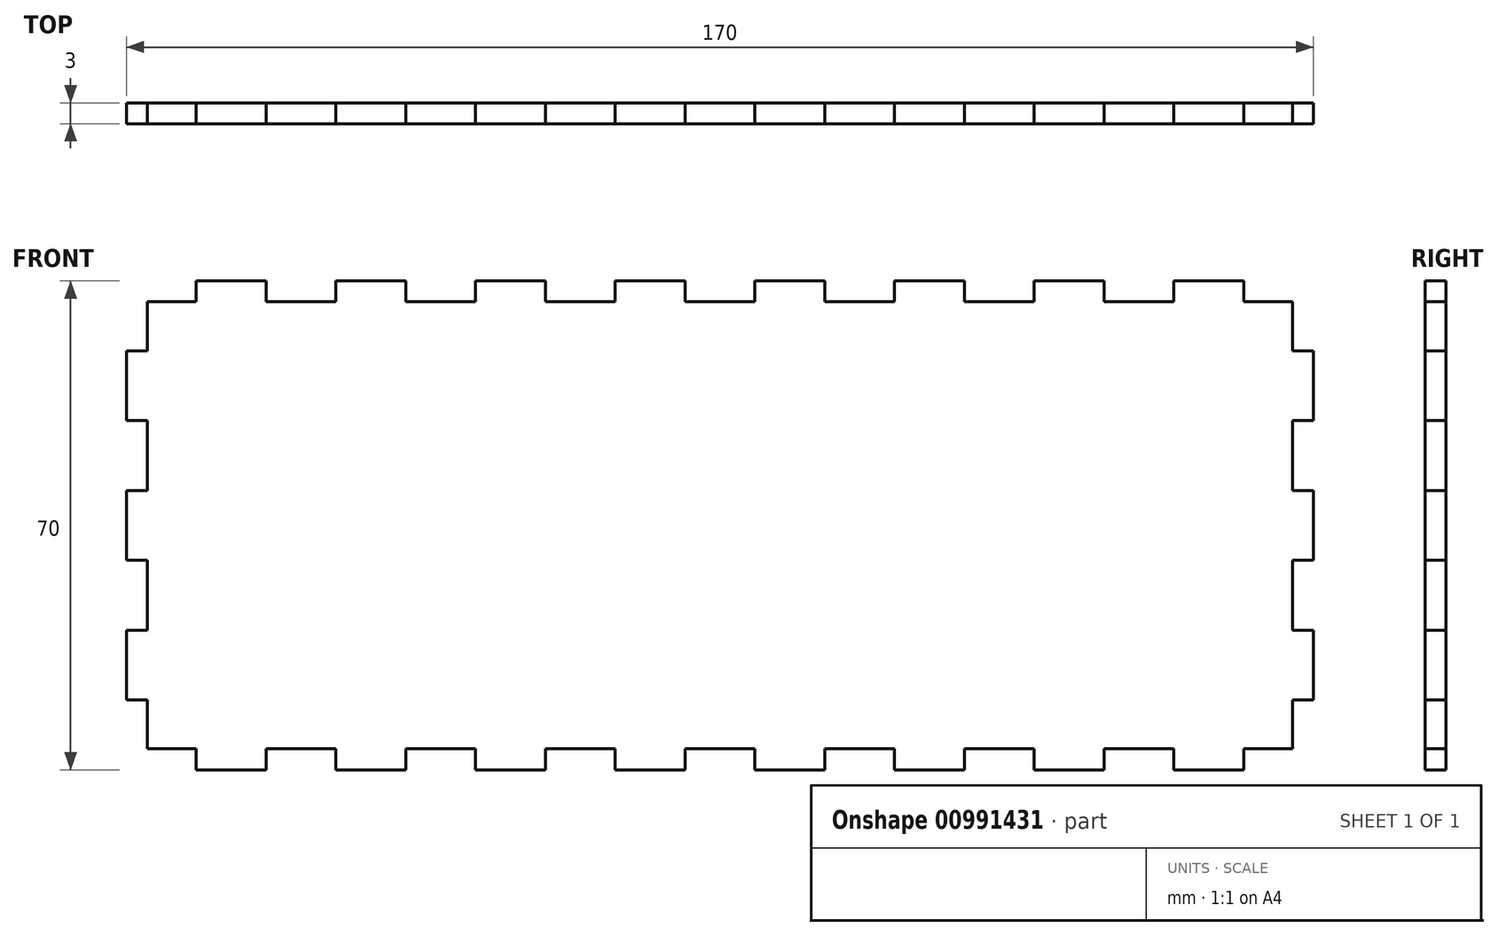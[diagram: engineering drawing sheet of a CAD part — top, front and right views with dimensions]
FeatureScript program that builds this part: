
annotation { "Feature Type Name" : "Feature", "Feature Type Description" : "" }
export const myFeature = defineFeature(function(context is Context, id is Id, definition is map)
    precondition{}
    {
        {
            var Q0;
            Q0=qCreatedBy(makeId("Front.planeOp"),FACE);
            var sketch = newSketch(context, id + "F0", { "sketchPlane" : qUnion([Q0])});
            skLineSegment(sketch, "E0.bottom", {"start": v(85, -35) * mm, "end": v(-85, -35) * mm});
            skLineSegment(sketch, "E0.top", {"start": v(85, 35) * mm, "end": v(-85, 35) * mm});
            skLineSegment(sketch, "E0.left", {"start": v(85, -35) * mm, "end": v(85, 35) * mm});
            skLineSegment(sketch, "E0.right", {"start": v(-85, -35) * mm, "end": v(-85, 35) * mm});
            skPoint(sketch, "E0.middle", {"position": v(0, 0) * mm});
            skSolve(sketch);
        }
        {
            var Q0;
            Q0=makeQuery(id+"F0.imprint","IMPRINT",FACE,{"disambiguationData":[TD([[makeQuery(id+"F0.imprint","IMPRINT",EDGE,{"derivedFrom":sQuery(id+"F0.wireOp",EDGE,"E0.bottom")}),-1.0]])]});
            extrude(context, id + "F1", {"entities" : qUnion([Q0]), "depth" : 3 * mm, "offsetDistance" : 25 * mm});
        }
        {
            var Q0;
            Q0=makeQuery(id+"F1.opExtrude","CAP_FACE",FACE,{"disambiguationData":[OSD([sQuery(id+"F0.wireOp",EDGE,"E0.bottom"),sQuery(id+"F0.wireOp",EDGE,"E0.top"),sQuery(id+"F0.wireOp",EDGE,"E0.left"),sQuery(id+"F0.wireOp",EDGE,"E0.right")])],"isStart":false});
            var sketch = newSketch(context, id + "F2", { "sketchPlane" : qUnion([Q0])});
            skLineSegment(sketch, "E1.bottom", {"start": v(-85, -35) * mm, "end": v(-75, -35) * mm});
            skLineSegment(sketch, "E1.top", {"start": v(-85, -32) * mm, "end": v(-75, -32) * mm});
            skLineSegment(sketch, "E1.left", {"start": v(-85, -35) * mm, "end": v(-85, -32) * mm});
            skLineSegment(sketch, "E1.right", {"start": v(-75, -35) * mm, "end": v(-75, -32) * mm});
            skLineSegment(sketch, "E2.1.0.0", {"start": v(-55, -35) * mm, "end": v(-55, -32) * mm});
            skLineSegment(sketch, "E2.1.0.1", {"start": v(-65, -35) * mm, "end": v(-65, -32) * mm});
            skLineSegment(sketch, "E2.1.0.2", {"start": v(-65, -35) * mm, "end": v(-55, -35) * mm});
            skLineSegment(sketch, "E2.1.0.3", {"start": v(-65, -32) * mm, "end": v(-55, -32) * mm});
            skLineSegment(sketch, "E2.2.0.0", {"start": v(-35, -35) * mm, "end": v(-35, -32) * mm});
            skLineSegment(sketch, "E2.2.0.1", {"start": v(-45, -35) * mm, "end": v(-45, -32) * mm});
            skLineSegment(sketch, "E2.2.0.2", {"start": v(-45, -35) * mm, "end": v(-35, -35) * mm});
            skLineSegment(sketch, "E2.2.0.3", {"start": v(-45, -32) * mm, "end": v(-35, -32) * mm});
            skLineSegment(sketch, "E2.3.0.0", {"start": v(-15, -35) * mm, "end": v(-15, -32) * mm});
            skLineSegment(sketch, "E2.3.0.1", {"start": v(-25, -35) * mm, "end": v(-25, -32) * mm});
            skLineSegment(sketch, "E2.3.0.2", {"start": v(-25, -35) * mm, "end": v(-15, -35) * mm});
            skLineSegment(sketch, "E2.3.0.3", {"start": v(-25, -32) * mm, "end": v(-15, -32) * mm});
            skLineSegment(sketch, "E2.4.0.0", {"start": v(5, -35) * mm, "end": v(5, -32) * mm});
            skLineSegment(sketch, "E2.4.0.1", {"start": v(-5, -35) * mm, "end": v(-5, -32) * mm});
            skLineSegment(sketch, "E2.4.0.2", {"start": v(-5, -35) * mm, "end": v(5, -35) * mm});
            skLineSegment(sketch, "E2.4.0.3", {"start": v(-5, -32) * mm, "end": v(5, -32) * mm});
            skLineSegment(sketch, "E2.5.0.0", {"start": v(25, -35) * mm, "end": v(25, -32) * mm});
            skLineSegment(sketch, "E2.5.0.1", {"start": v(15, -35) * mm, "end": v(15, -32) * mm});
            skLineSegment(sketch, "E2.5.0.2", {"start": v(15, -35) * mm, "end": v(25, -35) * mm});
            skLineSegment(sketch, "E2.5.0.3", {"start": v(15, -32) * mm, "end": v(25, -32) * mm});
            skLineSegment(sketch, "E2.6.0.0", {"start": v(45, -35) * mm, "end": v(45, -32) * mm});
            skLineSegment(sketch, "E2.6.0.1", {"start": v(35, -35) * mm, "end": v(35, -32) * mm});
            skLineSegment(sketch, "E2.6.0.2", {"start": v(35, -35) * mm, "end": v(45, -35) * mm});
            skLineSegment(sketch, "E2.6.0.3", {"start": v(35, -32) * mm, "end": v(45, -32) * mm});
            skLineSegment(sketch, "E2.7.0.0", {"start": v(65, -35) * mm, "end": v(65, -32) * mm});
            skLineSegment(sketch, "E2.7.0.1", {"start": v(55, -35) * mm, "end": v(55, -32) * mm});
            skLineSegment(sketch, "E2.7.0.2", {"start": v(55, -35) * mm, "end": v(65, -35) * mm});
            skLineSegment(sketch, "E2.7.0.3", {"start": v(55, -32) * mm, "end": v(65, -32) * mm});
            skLineSegment(sketch, "E2.8.0.0", {"start": v(85, -35) * mm, "end": v(85, -32) * mm});
            skLineSegment(sketch, "E2.8.0.1", {"start": v(75, -35) * mm, "end": v(75, -32) * mm});
            skLineSegment(sketch, "E2.8.0.2", {"start": v(75, -35) * mm, "end": v(85, -35) * mm});
            skLineSegment(sketch, "E2.8.0.3", {"start": v(75, -32) * mm, "end": v(85, -32) * mm});
            skLineSegment(sketch, "E2.direction1", {"start": v(-85, -35) * mm, "end": v(-65, -35) * mm, "construction": true});
            skLineSegment(sketch, "E3", {"start": v(-85, 0) * mm, "end": v(85, 0) * mm, "construction": true});
            skLineSegment(sketch, "E4.MirrorCS", {"start": v(-65, 35) * mm, "end": v(-65, 32) * mm});
            skLineSegment(sketch, "E5.MirrorCS", {"start": v(-25, 35) * mm, "end": v(-25, 32) * mm});
            skLineSegment(sketch, "E6.MirrorCS", {"start": v(-35, 35) * mm, "end": v(-35, 32) * mm});
            skLineSegment(sketch, "E7.MirrorCS", {"start": v(-5, 35) * mm, "end": v(-5, 32) * mm});
            skLineSegment(sketch, "E8.MirrorCS", {"start": v(-85, 35) * mm, "end": v(-85, 32) * mm});
            skLineSegment(sketch, "E9.MirrorCS", {"start": v(75, 35) * mm, "end": v(75, 32) * mm});
            skLineSegment(sketch, "E10.MirrorCS", {"start": v(25, 35) * mm, "end": v(25, 32) * mm});
            skLineSegment(sketch, "E11.MirrorCS", {"start": v(-45, 35) * mm, "end": v(-45, 32) * mm});
            skLineSegment(sketch, "E12.MirrorCS", {"start": v(45, 35) * mm, "end": v(45, 32) * mm});
            skLineSegment(sketch, "E13.MirrorCS", {"start": v(-55, 35) * mm, "end": v(-55, 32) * mm});
            skLineSegment(sketch, "E14.MirrorCS", {"start": v(85, 35) * mm, "end": v(85, 32) * mm});
            skLineSegment(sketch, "E15.MirrorCS", {"start": v(-15, 35) * mm, "end": v(-15, 32) * mm});
            skLineSegment(sketch, "E16.MirrorCS", {"start": v(55, 35) * mm, "end": v(55, 32) * mm});
            skLineSegment(sketch, "E17.MirrorCS", {"start": v(65, 35) * mm, "end": v(65, 32) * mm});
            skLineSegment(sketch, "E18.MirrorCS", {"start": v(15, 35) * mm, "end": v(15, 32) * mm});
            skLineSegment(sketch, "E19.MirrorCS", {"start": v(35, 35) * mm, "end": v(35, 32) * mm});
            skLineSegment(sketch, "E20.MirrorCS", {"start": v(5, 35) * mm, "end": v(5, 32) * mm});
            skLineSegment(sketch, "E21.MirrorCS", {"start": v(-75, 35) * mm, "end": v(-75, 32) * mm});
            skLineSegment(sketch, "E22.MirrorCS", {"start": v(-85, 35) * mm, "end": v(-75, 35) * mm});
            skLineSegment(sketch, "E23.MirrorCS", {"start": v(-25, 35) * mm, "end": v(-15, 35) * mm});
            skLineSegment(sketch, "E24.MirrorCS", {"start": v(55, 35) * mm, "end": v(65, 35) * mm});
            skLineSegment(sketch, "E25.MirrorCS", {"start": v(-25, 32) * mm, "end": v(-15, 32) * mm});
            skLineSegment(sketch, "E26.MirrorCS", {"start": v(35, 32) * mm, "end": v(45, 32) * mm});
            skLineSegment(sketch, "E27.MirrorCS", {"start": v(55, 32) * mm, "end": v(65, 32) * mm});
            skLineSegment(sketch, "E28.MirrorCS", {"start": v(15, 35) * mm, "end": v(25, 35) * mm});
            skLineSegment(sketch, "E29.MirrorCS", {"start": v(-65, 32) * mm, "end": v(-55, 32) * mm});
            skLineSegment(sketch, "E30.MirrorCS", {"start": v(35, 35) * mm, "end": v(45, 35) * mm});
            skLineSegment(sketch, "E31.MirrorCS", {"start": v(-45, 35) * mm, "end": v(-35, 35) * mm});
            skLineSegment(sketch, "E32.MirrorCS", {"start": v(75, 32) * mm, "end": v(85, 32) * mm});
            skLineSegment(sketch, "E33.MirrorCS", {"start": v(-5, 32) * mm, "end": v(5, 32) * mm});
            skLineSegment(sketch, "E34.MirrorCS", {"start": v(-65, 35) * mm, "end": v(-55, 35) * mm});
            skLineSegment(sketch, "E35.MirrorCS", {"start": v(-85, 35) * mm, "end": v(-65, 35) * mm, "construction": true});
            skLineSegment(sketch, "E36.MirrorCS", {"start": v(-45, 32) * mm, "end": v(-35, 32) * mm});
            skLineSegment(sketch, "E37.MirrorCS", {"start": v(-5, 35) * mm, "end": v(5, 35) * mm});
            skLineSegment(sketch, "E38.MirrorCS", {"start": v(-85, 32) * mm, "end": v(-75, 32) * mm});
            skLineSegment(sketch, "E39.MirrorCS", {"start": v(75, 35) * mm, "end": v(85, 35) * mm});
            skLineSegment(sketch, "E40.MirrorCS", {"start": v(15, 32) * mm, "end": v(25, 32) * mm});
            skLineSegment(sketch, "E41.bottom", {"start": v(-85, 35) * mm, "end": v(-82, 35) * mm});
            skLineSegment(sketch, "E41.top", {"start": v(-85, 25) * mm, "end": v(-82, 25) * mm});
            skLineSegment(sketch, "E41.left", {"start": v(-85, 35) * mm, "end": v(-85, 25) * mm});
            skLineSegment(sketch, "E41.right", {"start": v(-82, 35) * mm, "end": v(-82, 25) * mm});
            skLineSegment(sketch, "E42.0.1.0", {"start": v(-82, 15) * mm, "end": v(-82, 5) * mm});
            skLineSegment(sketch, "E42.0.1.1", {"start": v(-85, 15) * mm, "end": v(-85, 5) * mm});
            skLineSegment(sketch, "E42.0.1.2", {"start": v(-85, 5) * mm, "end": v(-82, 5) * mm});
            skLineSegment(sketch, "E42.0.1.3", {"start": v(-85, 15) * mm, "end": v(-82, 15) * mm});
            skLineSegment(sketch, "E42.0.1.4", {"start": v(-85, 15) * mm, "end": v(-85, 12) * mm});
            skLineSegment(sketch, "E42.0.2.0", {"start": v(-82, -5) * mm, "end": v(-82, -15) * mm});
            skLineSegment(sketch, "E42.0.2.1", {"start": v(-85, -5) * mm, "end": v(-85, -15) * mm});
            skLineSegment(sketch, "E42.0.2.2", {"start": v(-85, -15) * mm, "end": v(-82, -15) * mm});
            skLineSegment(sketch, "E42.0.2.3", {"start": v(-85, -5) * mm, "end": v(-82, -5) * mm});
            skLineSegment(sketch, "E42.0.2.4", {"start": v(-85, -5) * mm, "end": v(-85, -8) * mm});
            skLineSegment(sketch, "E42.0.3.0", {"start": v(-82, -25) * mm, "end": v(-82, -35) * mm});
            skLineSegment(sketch, "E42.0.3.1", {"start": v(-85, -25) * mm, "end": v(-85, -35) * mm});
            skLineSegment(sketch, "E42.0.3.2", {"start": v(-85, -35) * mm, "end": v(-82, -35) * mm});
            skLineSegment(sketch, "E42.0.3.3", {"start": v(-85, -25) * mm, "end": v(-82, -25) * mm});
            skLineSegment(sketch, "E42.0.3.4", {"start": v(-85, -25) * mm, "end": v(-85, -28) * mm});
            skLineSegment(sketch, "E42.direction1", {"start": v(-85, 25) * mm, "end": v(-60, 25) * mm, "construction": true});
            skLineSegment(sketch, "E42.direction2", {"start": v(-85, 25) * mm, "end": v(-85, 5) * mm, "construction": true});
            skLineSegment(sketch, "E43", {"start": v(0, 35) * mm, "end": v(0, -35) * mm, "construction": true});
            skLineSegment(sketch, "E44.MirrorCS", {"start": v(85, -25) * mm, "end": v(85, -28) * mm});
            skLineSegment(sketch, "E45.MirrorCS", {"start": v(85, 15) * mm, "end": v(85, 12) * mm});
            skLineSegment(sketch, "E46.MirrorCS", {"start": v(85, -5) * mm, "end": v(85, -8) * mm});
            skLineSegment(sketch, "E47.MirrorCS", {"start": v(85, 15) * mm, "end": v(85, 5) * mm});
            skLineSegment(sketch, "E48.MirrorCS", {"start": v(85, 5) * mm, "end": v(82, 5) * mm});
            skLineSegment(sketch, "E49.MirrorCS", {"start": v(82, 15) * mm, "end": v(82, 5) * mm});
            skLineSegment(sketch, "E50.MirrorCS", {"start": v(85, -35) * mm, "end": v(82, -35) * mm});
            skLineSegment(sketch, "E51.MirrorCS", {"start": v(85, -5) * mm, "end": v(85, -15) * mm});
            skLineSegment(sketch, "E52.MirrorCS", {"start": v(85, 35) * mm, "end": v(82, 35) * mm});
            skLineSegment(sketch, "E53.MirrorCS", {"start": v(85, 25) * mm, "end": v(85, 5) * mm, "construction": true});
            skLineSegment(sketch, "E54.MirrorCS", {"start": v(82, -25) * mm, "end": v(82, -35) * mm});
            skLineSegment(sketch, "E55.MirrorCS", {"start": v(85, 15) * mm, "end": v(82, 15) * mm});
            skLineSegment(sketch, "E56.MirrorCS", {"start": v(85, -15) * mm, "end": v(82, -15) * mm});
            skLineSegment(sketch, "E57.MirrorCS", {"start": v(85, -25) * mm, "end": v(82, -25) * mm});
            skLineSegment(sketch, "E58.MirrorCS", {"start": v(85, 25) * mm, "end": v(82, 25) * mm});
            skLineSegment(sketch, "E59.MirrorCS", {"start": v(82, 35) * mm, "end": v(82, 25) * mm});
            skLineSegment(sketch, "E60.MirrorCS", {"start": v(85, 35) * mm, "end": v(85, 25) * mm});
            skLineSegment(sketch, "E61.MirrorCS", {"start": v(85, -25) * mm, "end": v(85, -35) * mm});
            skLineSegment(sketch, "E62.MirrorCS", {"start": v(85, -5) * mm, "end": v(82, -5) * mm});
            skLineSegment(sketch, "E63.MirrorCS", {"start": v(82, -5) * mm, "end": v(82, -15) * mm});
            skSolve(sketch);
        }
        {
            var Q0;
            Q0=qSketchRegion(id+"F2",true);
            extrude(context, id + "F3", {"entities" : qUnion([Q0]), "operationType" : NewBodyOperationType.REMOVE, "endBound" : BoundingType.THROUGH_ALL, "oppositeDirection" : true, "depth" : 25 * mm, "offsetDistance" : 25 * mm});
        }
    });
